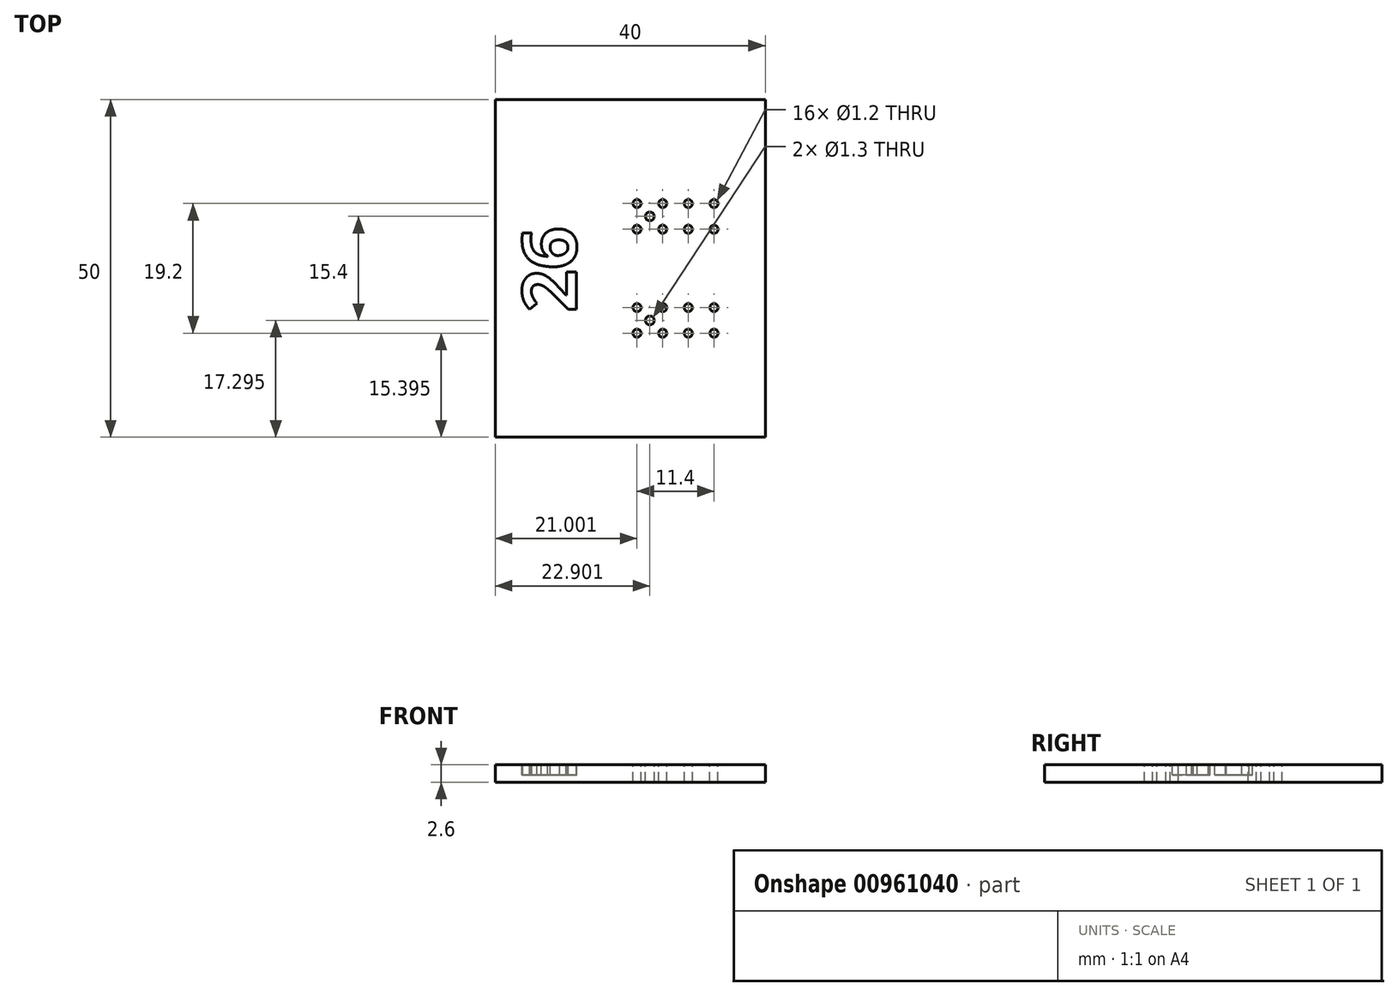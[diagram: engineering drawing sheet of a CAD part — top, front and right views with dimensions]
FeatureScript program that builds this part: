
annotation { "Feature Type Name" : "Feature", "Feature Type Description" : "" }
export const myFeature = defineFeature(function(context is Context, id is Id, definition is map)
    precondition{}
    {
        {
            var Q0;
            Q0=qCreatedBy(makeId("Top.planeOp"),FACE);
            var sketch = newSketch(context, id + "F0", { "sketchPlane" : qUnion([Q0])});
            skLineSegment(sketch, "E0.bottom", {"start": v(-43.16, 28.34) * mm, "end": v(-3.16, 28.34) * mm});
            skLineSegment(sketch, "E0.top", {"start": v(-43.16, -21.66) * mm, "end": v(-3.16, -21.66) * mm});
            skLineSegment(sketch, "E0.left", {"start": v(-43.16, 28.34) * mm, "end": v(-43.16, -21.66) * mm});
            skLineSegment(sketch, "E0.right", {"start": v(-3.16, 28.34) * mm, "end": v(-3.16, -21.66) * mm});
            skSolve(sketch);
        }
        {
            var Q0;
            Q0=makeQuery(id+"F0.imprint","IMPRINT",FACE,{"disambiguationData":[TD([[makeQuery(id+"F0.imprint","IMPRINT",EDGE,{"derivedFrom":sQuery(id+"F0.wireOp",EDGE,"E0.bottom")}),-1.0]])]});
            extrude(context, id + "F1", {"entities" : qUnion([Q0]), "depth" : 2.6 * mm, "offsetDistance" : 25 * mm});
        }
        {
            var Q0;
            Q0=makeQuery(id+"F1.opExtrude","CAP_FACE",FACE,{"disambiguationData":[OSD([sQuery(id+"F0.wireOp",EDGE,"E0.bottom"),sQuery(id+"F0.wireOp",EDGE,"E0.top"),sQuery(id+"F0.wireOp",EDGE,"E0.left"),sQuery(id+"F0.wireOp",EDGE,"E0.right")])],"isStart":false});
            var sketch = newSketch(context, id + "F2", { "sketchPlane" : qUnion([Q0])});
            skText(sketch, "E1", { "text": "26", "fontName": "OpenSans-Bold.ttf"});
            const initialGuessF2  = {"E1": [-0.03116, -0.00316, 0, 1, 0.008]};
            skSetInitialGuess(sketch, initialGuessF2);
            skSolve(sketch);
        }
        {
            var Q0;
            Q0=qSketchRegion(id+"F2",true);
            extrude(context, id + "F3", {"entities" : qUnion([Q0]), "operationType" : NewBodyOperationType.REMOVE, "oppositeDirection" : true, "depth" : 1.5 * mm, "offsetDistance" : 25 * mm});
        }
        {
            var Q0;
            {var subQ0=sQuery(id+"F0.wireOp",EDGE,"E0.left");var subQ1=sQuery(id+"F0.wireOp",EDGE,"E0.bottom");var subQ2=sQuery(id+"F0.wireOp",EDGE,"E0.right");var subQ3=sQuery(id+"F0.wireOp",EDGE,"E0.top");Q0=makeQuery(id+"F3.boolean.opBoolean","SPLIT",FACE,{"disambiguationData":[TD([makeQuery(id+"F1.opExtrude","SWEPT_FACE",FACE,{"disambiguationData":[OSD([subQ1])]})])],"derivedFrom":makeQuery(id+"F1.opExtrude","CAP_FACE",FACE,{"disambiguationData":[OSD([subQ1,subQ3,subQ0,subQ2])],"isStart":false})});}
            var sketch = newSketch(context, id + "F4", { "sketchPlane" : qUnion([Q0])});
            skCircle(sketch, "E2", {"center": v(-22.16, -2.46) * mm, "radius": 0.6 * mm});
            skCircle(sketch, "E3", {"center": v(-18.36, -2.46) * mm, "radius": 0.6 * mm});
            skCircle(sketch, "E4", {"center": v(-14.56, -2.46) * mm, "radius": 0.6 * mm});
            skCircle(sketch, "E5", {"center": v(-10.76, -2.46) * mm, "radius": 0.6 * mm});
            skCircle(sketch, "E6", {"center": v(-22.16, -6.26) * mm, "radius": 0.6 * mm});
            skCircle(sketch, "E7", {"center": v(-18.36, -6.26) * mm, "radius": 0.6 * mm});
            skCircle(sketch, "E8", {"center": v(-14.56, -6.26) * mm, "radius": 0.6 * mm});
            skCircle(sketch, "E9", {"center": v(-10.76, -6.26) * mm, "radius": 0.6 * mm});
            skCircle(sketch, "E10", {"center": v(-20.26, -4.36) * mm, "radius": 0.65 * mm});
            skCircle(sketch, "E11", {"center": v(-22.16, 12.94) * mm, "radius": 0.6 * mm});
            skCircle(sketch, "E12", {"center": v(-18.36, 12.94) * mm, "radius": 0.6 * mm});
            skCircle(sketch, "E13", {"center": v(-14.56, 12.94) * mm, "radius": 0.6 * mm});
            skCircle(sketch, "E14", {"center": v(-10.76, 12.94) * mm, "radius": 0.6 * mm});
            skCircle(sketch, "E15", {"center": v(-22.16, 9.14) * mm, "radius": 0.6 * mm});
            skCircle(sketch, "E16", {"center": v(-18.36, 9.14) * mm, "radius": 0.6 * mm});
            skCircle(sketch, "E17", {"center": v(-14.56, 9.14) * mm, "radius": 0.6 * mm});
            skCircle(sketch, "E18", {"center": v(-10.76, 9.14) * mm, "radius": 0.6 * mm});
            skCircle(sketch, "E19", {"center": v(-20.26, 11.04) * mm, "radius": 0.65 * mm});
            skSolve(sketch);
        }
        {
            var Q0;
            Q0 = qSketchRegion(id + "F4", true);
            extrude(context, id + "F5", {"entities" : qUnion([Q0]), "operationType" : NewBodyOperationType.REMOVE, "endBound" : BoundingType.UP_TO_NEXT, "oppositeDirection" : true, "depth" : 25 * mm, "offsetDistance" : 25 * mm});
        }
    });
